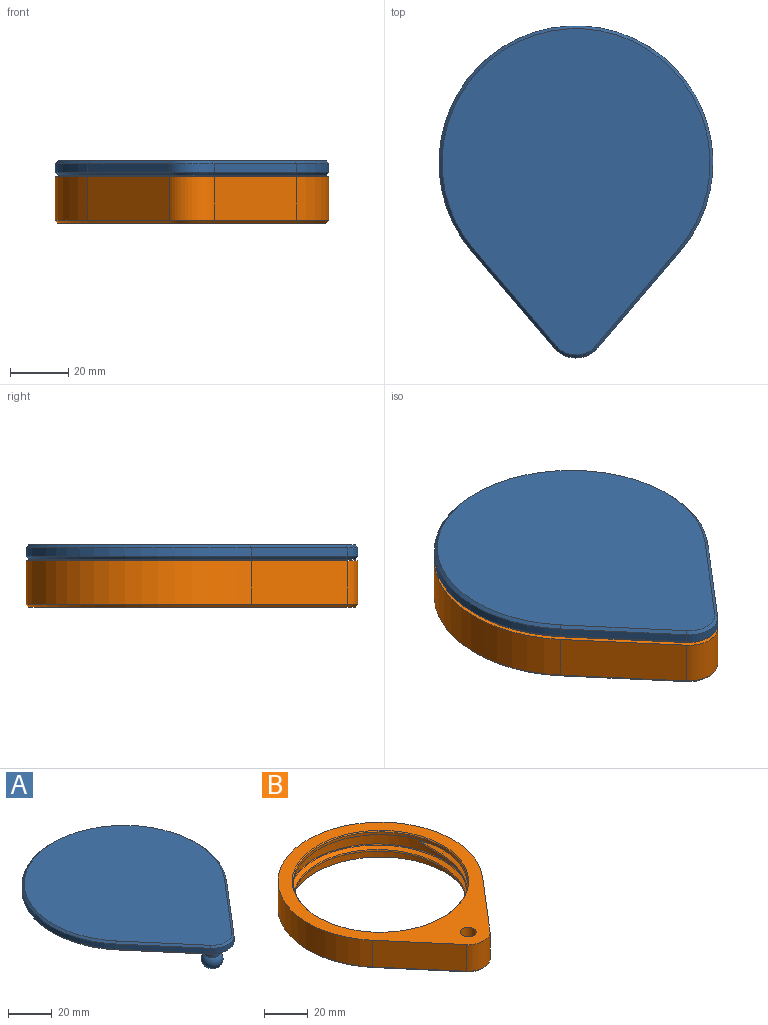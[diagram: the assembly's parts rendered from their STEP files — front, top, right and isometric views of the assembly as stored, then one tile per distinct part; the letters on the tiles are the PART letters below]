
ASSEMBLY  parts=2 mates=1
PART A: 18 faces, bbox 94x114x17.8 mm
  f0: cylinder r=10mm len=15.21mm, axis (0,0,-1), area 51.9mm2, adj f1,f3,f11,f15
  f1: plane 32.98x28.15mm, normal (0.76,-0.65,0), area 130.1mm2, adj f0,f2,f10,f14
  f2: cylinder r=47mm len=94mm, axis (0,0,-1), area 642.2mm2, adj f1,f3,f8,f12
  f3: plane 32.98x28.15mm, normal (-0.76,-0.65,0), area 130.1mm2, adj f0,f2,f9,f13
  f4: plane 112x92mm, normal (0,0,1), area 7273.4mm2, adj f12,f13,f14,f15
  f5: plane 112x92mm, normal (0,0,-1), area 2210.1mm2, adj f6,f8,f9,f10,f11,f16
  f6: cylinder r=3.42mm len=6.84mm, axis (0,0,1), area 125.9mm2, adj f5,f7
  f7: torus R=1.12mm, axis (0,0,1), area 239.2mm2, adj f6
  f8: cone r=47mm half-angle=45deg, axis (0,0,1), area 299.5mm2, adj f2,f5,f9,f10
  f9: plane 33.63x28.91mm, normal (-0.54,-0.46,-0.71), area 61.3mm2, adj f3,f5,f8,f11
  f10: plane 33.63x28.91mm, normal (0.54,-0.46,-0.71), area 61.3mm2, adj f1,f5,f8,f11
  f11: cone r=10mm half-angle=45deg, axis (0,0,1), area 23.2mm2, adj f0,f5,f9,f10
  f12: cone r=46mm half-angle=45deg, axis (0,0,-1), area 299.5mm2, adj f2,f4,f13,f14
  f13: plane 33.63x28.91mm, normal (-0.54,-0.46,0.71), area 61.3mm2, adj f3,f4,f12,f15
  f14: plane 33.63x28.91mm, normal (0.54,-0.46,0.71), area 61.3mm2, adj f1,f4,f12,f15
  f15: cone r=9mm half-angle=45deg, axis (0,0,-1), area 23.2mm2, adj f0,f4,f13,f14
  f16: cone r=40mm half-angle=15deg, axis (0,0,1), area 259.3mm2, adj f5,f17
  f17: plane 79.46x79.46mm, normal (0,0,-1), area 4959.4mm2, adj f16
PART B: 32 faces, bbox 94x115.5x16 mm
  f0: cylinder r=42mm len=84mm, axis (0,0,-1), area 1102.1mm2, adj f1,f16,f25,f26,f27,f28,f29,f30
  f1: plane 84x84mm, normal (0,0,-1), area 515.2mm2, adj f0,f2
  f2: cylinder r=40mm len=80mm, axis (0,0,-1), area 377mm2, adj f1,f3
  f3: cone r=40mm half-angle=45deg, axis (0,0,1), area 178.8mm2, adj f2,f4
  f4: plane 114x94mm, normal (0,0,1), area 2391.9mm2, adj f3,f5,f11,f12,f13,f14
  f5: cylinder r=10mm len=15.21mm, axis (0,0,-1), area 259.3mm2, adj f4,f6,f11,f13
  f6: cone r=10mm half-angle=45deg, axis (0,0,1), area 23.2mm2, adj f5,f7,f9,f10
  f7: plane 33.63x28.91mm, normal (0.54,-0.46,-0.71), area 61.3mm2, adj f6,f8,f9,f13
  f8: cone r=47mm half-angle=45deg, axis (0,0,1), area 299.5mm2, adj f7,f9,f10,f12
  f9: plane 112x92mm, normal (0,0,-1), area 1731.6mm2, adj f6,f7,f8,f10,f25
  f10: plane 33.63x28.91mm, normal (-0.54,-0.46,-0.71), area 61.3mm2, adj f6,f8,f9,f11
  f11: plane 32.98x28.15mm, normal (-0.76,-0.65,0), area 650.4mm2, adj f4,f5,f10,f12
  f12: cylinder r=47mm len=94mm, axis (0,0,-1), area 3210.9mm2, adj f4,f8,f11,f13
  f13: plane 32.98x28.15mm, normal (0.76,-0.65,0), area 650.4mm2, adj f4,f5,f7,f12
  f14: cylinder r=3.72mm len=7.44mm, axis (0,0,1), area 124.1mm2, adj f4,f15
  f15: torus R=1.12mm, axis (0,0,1), area 268.1mm2, adj f14
  f16: bspline ~97x84.06mm, area 166.2mm2, adj f0,f17,f24,f25,f31
  f17: extruded ~4.38x1.5mm, area 1.2mm2, adj f16,f18,f25
  f18: plane 13.55x3.86mm, normal (-0.16,0.47,0.87), area 22.7mm2, adj f17,f19,f24,f25
  f19: extruded ~13.78x4.25mm, area 14.7mm2, adj f18,f20,f22,f25
  f20: bspline ~91.8x79.51mm, area 313.8mm2, adj f19,f21,f24,f29
  f21: bspline ~96.42x83.54mm, area 712.5mm2, adj f20,f22,f26,f28
  f22: plane 13.64x3.87mm, normal (-0.12,0.49,-0.87), area 22.8mm2, adj f19,f21,f23,f25
  f23: extruded ~4.54x1.55mm, area 1.2mm2, adj f22,f25,f26
  f24: bspline ~96.42x83.54mm, area 712.5mm2, adj f16,f18,f20,f30
  f25: cylinder r=42mm len=84mm, axis (0,0,-1), area 1230.1mm2, adj f0,f9,f16,f17,f18,f19,f22,f23
  f26: bspline ~97x84.06mm, area 166.2mm2, adj f0,f21,f23,f25,f27
  f27: cylinder r=0.5mm len=4.55mm, axis (0,-1,-0.02), area 1.2mm2, adj f0,f26,f28
  f28: plane 13.55x2mm, normal (-0.5,0.02,-0.87), area 22.7mm2, adj f0,f21,f27,f29
  f29: cylinder r=0.5mm len=14.3mm, axis (0,-1,-0.02), area 14.7mm2, adj f0,f20,f28,f30
  f30: plane 13.6x2mm, normal (-0.5,-0.02,0.87), area 22.8mm2, adj f0,f24,f29,f31
  f31: cylinder r=0.5mm len=4.62mm, axis (0,-1,-0.02), area 1.2mm2, adj f0,f16,f30
PLACE A rot(axis=(0,0,-1),0deg) t=(19.23,11.99,5.23)mm
PLACE B t=(19.18,11.99,5.23)mm fixed
MATE revolute B.f14 <-> A.f0  axis (0,0,1) through (19.18,-45.01,26.63)mm
